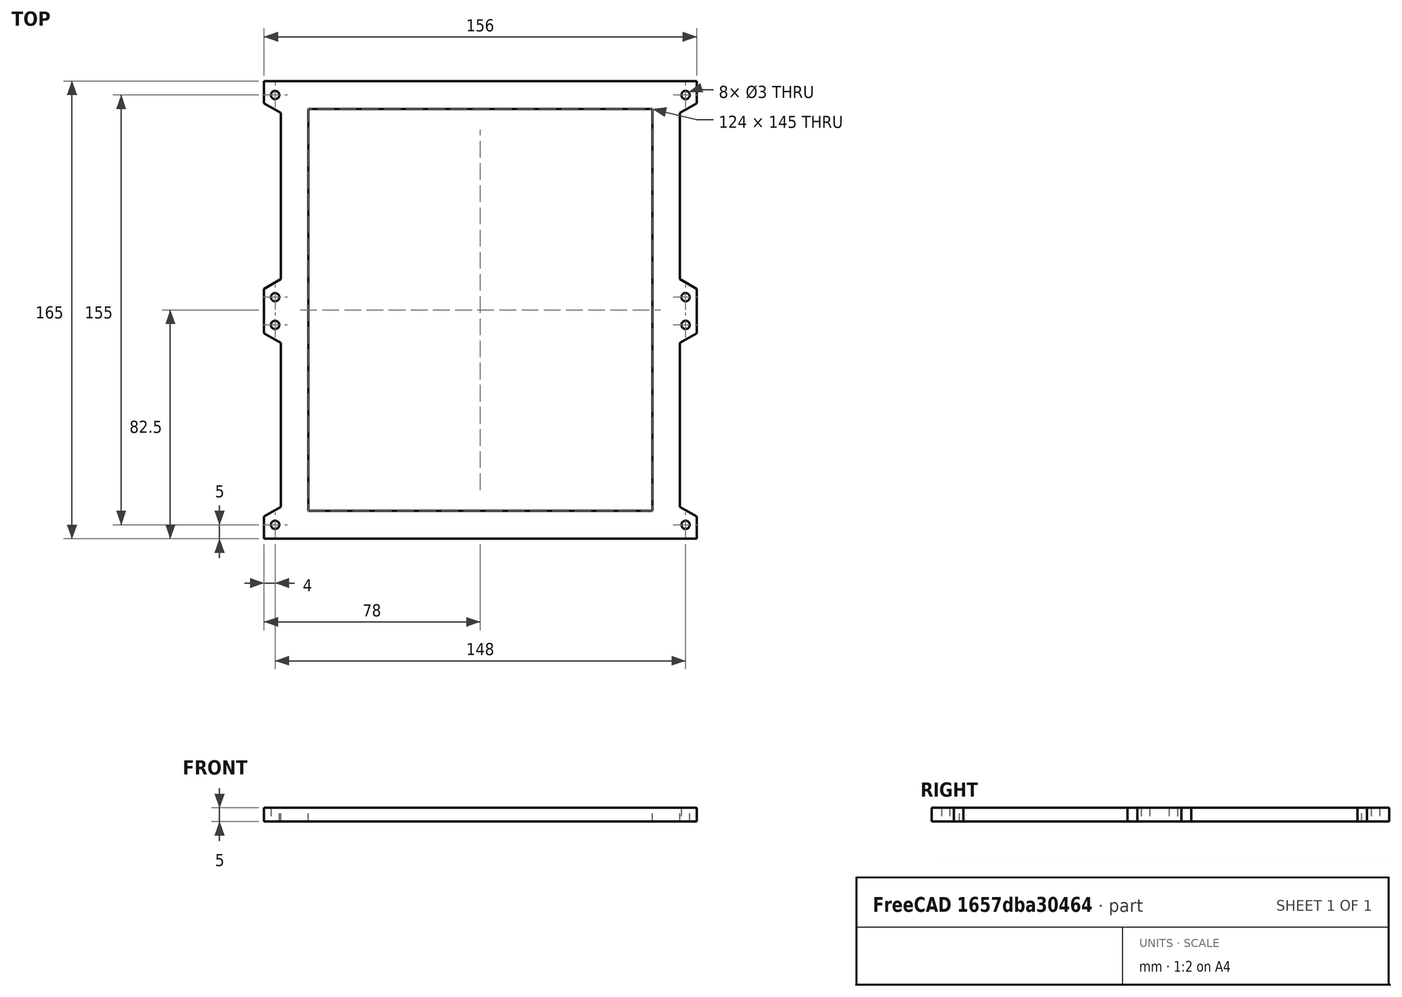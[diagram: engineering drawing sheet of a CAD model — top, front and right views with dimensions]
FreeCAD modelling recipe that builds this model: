
FCSTD DOCUMENT  (FreeCAD 0.15R4671 (Git))
Label: panel-cover
License: CC-BY 3.0
LicenseURL: http://creativecommons.org/licenses/by/3.0/
objects: Sketcher::SketchObject×1, PartDesign::Pad×1, Part::Feature×1
note: 4 computed .brp shape members not serialized (recipe doc carries the construction recipe); baked Part::Feature solids carry a one-line shape summary decoded from their .brp

FEATURE [Sketcher::SketchObject] Sketch001  label="Panel Cover Pad Sketch"
  sketch-geometry (33):
    g0: LineSegment StartX=0 StartY=0 StartZ=0 EndX=0 EndY=8 EndZ=0
    g1: LineSegment StartX=0 StartY=8 StartZ=0 EndX=6 EndY=11.4641 EndZ=0
    g2: LineSegment StartX=6 StartY=11.4641 StartZ=0 EndX=6 EndY=70.6359 EndZ=0
    g3: LineSegment StartX=6 StartY=70.6359 StartZ=0 EndX=0 EndY=74.1 EndZ=0
    g4: LineSegment StartX=0 StartY=74.1 StartZ=0 EndX=0 EndY=90.1 EndZ=0
    g5: LineSegment StartX=0 StartY=90.1 StartZ=0 EndX=6 EndY=93.5641 EndZ=0
    g6: LineSegment StartX=6 StartY=93.5641 StartZ=0 EndX=6 EndY=153.536 EndZ=0
    g7: LineSegment StartX=6 StartY=153.536 StartZ=0 EndX=0 EndY=157 EndZ=0
    g8: LineSegment StartX=0 StartY=157 StartZ=0 EndX=0 EndY=165 EndZ=0
    g9: LineSegment StartX=0 StartY=165 StartZ=0 EndX=156 EndY=165 EndZ=0
    g10: LineSegment StartX=156 StartY=165 StartZ=0 EndX=156 EndY=157 EndZ=0
    g11: LineSegment StartX=156 StartY=157 StartZ=0 EndX=150 EndY=153.536 EndZ=0
    g12: LineSegment StartX=150 StartY=153.536 StartZ=0 EndX=150 EndY=93.5641 EndZ=0
    g13: LineSegment StartX=150 StartY=93.5641 StartZ=0 EndX=156 EndY=90.1 EndZ=0
    g14: LineSegment StartX=156 StartY=90.1 StartZ=0 EndX=156 EndY=74.1 EndZ=0
    g15: LineSegment StartX=156 StartY=74.1 StartZ=0 EndX=150 EndY=70.6359 EndZ=0
    g16: LineSegment StartX=150 StartY=70.6359 StartZ=0 EndX=150 EndY=11.4641 EndZ=0
    g17: LineSegment StartX=150 StartY=11.4641 StartZ=0 EndX=156 EndY=8 EndZ=0
    g18: LineSegment StartX=156 StartY=8 StartZ=0 EndX=156 EndY=0 EndZ=0
    g19: LineSegment StartX=156 StartY=0 StartZ=0 EndX=0 EndY=0 EndZ=0
    g20: LineSegment [constr] StartX=-65 StartY=82.1 StartZ=0 EndX=235 EndY=82.1 EndZ=0
    g21: Circle CenterX=4 CenterY=5 CenterZ=0 NormalX=0 NormalY=0 NormalZ=1 Radius=1.5
    g22: Circle CenterX=152 CenterY=5 CenterZ=0 NormalX=0 NormalY=0 NormalZ=1 Radius=1.5
    g23: Circle CenterX=4 CenterY=87.1 CenterZ=0 NormalX=0 NormalY=0 NormalZ=1 Radius=1.5
    g24: Circle CenterX=4 CenterY=77.1 CenterZ=0 NormalX=0 NormalY=0 NormalZ=1 Radius=1.5
    g25: Circle CenterX=4 CenterY=160 CenterZ=0 NormalX=0 NormalY=0 NormalZ=1 Radius=1.5
    g26: Circle CenterX=152 CenterY=160 CenterZ=0 NormalX=0 NormalY=0 NormalZ=1 Radius=1.5
    g27: Circle CenterX=152 CenterY=87.1 CenterZ=0 NormalX=0 NormalY=0 NormalZ=1 Radius=1.5
    g28: Circle CenterX=152 CenterY=77.1 CenterZ=0 NormalX=0 NormalY=0 NormalZ=1 Radius=1.5
    g29: LineSegment StartX=16 StartY=10 StartZ=0 EndX=140 EndY=10 EndZ=0
    g30: LineSegment StartX=140 StartY=10 StartZ=0 EndX=140 EndY=155 EndZ=0
    g31: LineSegment StartX=140 StartY=155 StartZ=0 EndX=16 EndY=155 EndZ=0
    g32: LineSegment StartX=16 StartY=155 StartZ=0 EndX=16 EndY=10 EndZ=0
  constraints (97):
    c: Coincident(g-1,g0)
    c: Coincident(g0,g1)
    c: Coincident(g1,g2)
    c: Coincident(g2,g3)
    c: Coincident(g3,g4)
    c: Coincident(g4,g5)
    c: Coincident(g5,g6)
    c: Vertical(g6)
    c: Coincident(g6,g7)
    c: Vertical(g8)
    c: Coincident(g8,g9)
    c: Horizontal(g9)
    c: Coincident(g9,g10)
    c: Vertical(g10)
    c: Coincident(g10,g11)
    c: Coincident(g11,g12)
    c: Vertical(g12)
    c: Coincident(g12,g13)
    c: Coincident(g13,g14)
    c: Vertical(g14)
    c: Coincident(g14,g15)
    c: Coincident(g15,g16)
    c: Vertical(g16)
    c: Coincident(g16,g17)
    c: Coincident(g17,g18)
    c: PointOnObject(g18,g-1)
    c: Vertical(g18)
    c: Coincident(g18,g19)
    c: Coincident(g19,g0)
    c: Vertical(g0)
    c: Angle(g2,g1) = 2.0944
    c: Distance(g19) = 156
    c: Distance(g9) = 156
    c: PointOnObject(g8,g-2)
    c: DistanceY(g10) = -8
    c: DistanceY(g8) = 8
    c: Angle(g12,g11) = 2.0944
    c: Angle(g7,g6) = 2.0944
    c: DistanceX(g6,g7) = -6
    c: DistanceX(g11,g10) = 6
    c: DistanceY(g18,g9) = 165
    c: DistanceX(g17,g16) = -6
    c: Angle(g17,g16) = 2.0944
    c: Angle(g16,g15) = 2.0944
    c: Angle(g13,g12) = 2.0944
    c: Angle(g6,g5) = 2.0944
    c: Angle(g3,g2) = 2.0944
    c: DistanceY(g18,g17) = 8
    c: DistanceY(g14,g13) = 16
    c: DistanceY(g4) = 16
    c: DistanceY(g-1,g20) = 82.1
    c: Symmetric(g4,g3,g20)
    c: Symmetric(g13,g14,g20)
    c: Vertical(g2)
    c: DistanceX(g13,g12) = -6
    c: DistanceX(g3,g2) = 6
    c: DistanceX(g4,g5) = 6
    c: Coincident(g7,g8)
    c: DistanceX(g20) = 300
    c: DistanceY(g0) = 8
    c: DistanceX(g-1,g20) = -65
    c: DistanceY(g7,g25) = 3
    c: DistanceX(g7,g25) = 4
    c: DistanceX(g10,g26) = -4
    c: DistanceY(g10,g26) = 3
    c: DistanceY(g27,g13) = 3
    c: DistanceX(g27,g13) = 4
    c: DistanceX(g14,g28) = -4
    c: DistanceY(g28,g14) = -3
    c: DistanceX(g22,g17) = 4
    c: DistanceY(g17,g22) = -3
    c: DistanceY(g21,g0) = 3
    c: DistanceX(g21,g0) = -4
    c: DistanceY(g24,g3) = -3
    c: DistanceX(g24,g3) = -4
    c: DistanceY(g4,g23) = -3
    c: DistanceX(g23,g4) = -4
    c: Radius(g21) = 1.5
    c: Equal(g21,g22)
    c: Equal(g22,g28)
    c: Equal(g28,g27)
    c: Equal(g27,g26)
    c: Equal(g26,g25)
    c: Equal(g25,g23)
    c: Equal(g23,g24)
    c: Coincident(g29,g30)
    c: Coincident(g30,g31)
    c: Coincident(g31,g32)
    c: Coincident(g32,g29)
    c: Horizontal(g29)
    c: Horizontal(g31)
    c: Vertical(g30)
    c: Vertical(g32)
    c: DistanceX(g-1,g29) = 16
    c: DistanceY(g-1,g29) = 10
    c: DistanceX(g29,g18) = 16
    c: DistanceY(g30,g9) = 10
FEATURE [PartDesign::Pad] Pad  label="Panel Cover Pad"
  Length = 5
  Length2 = 100
  Sketch = -> Sketch001
  Type = 0
FEATURE [Part::Feature] Pad001  label="PanelCover"
  shape: bbox 156 x 165 x 5 mm, 34 faces (baked)
